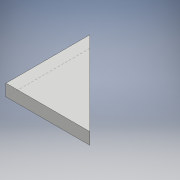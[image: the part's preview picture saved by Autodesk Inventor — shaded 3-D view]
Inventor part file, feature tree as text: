
AUTODESK INVENTOR PART (.ipt)
format: ipt  version: 2018 (Build 220112000, 112)  size: 90,112 bytes
history: native  units: mm
features: other x1, extrude x1, sketch x1
ambient origin geometry x8: Origin, YZ Plane, XZ Plane, XY Plane, X Axis, Y Axis, Z Axis, Center Point
bodies: Body1 (feature_tree)
feature tree (3):
  other  "ソリッド1"
  extrude  "押し出し1"  Depth=32.0mm
  sketch  "スケッチ1"
